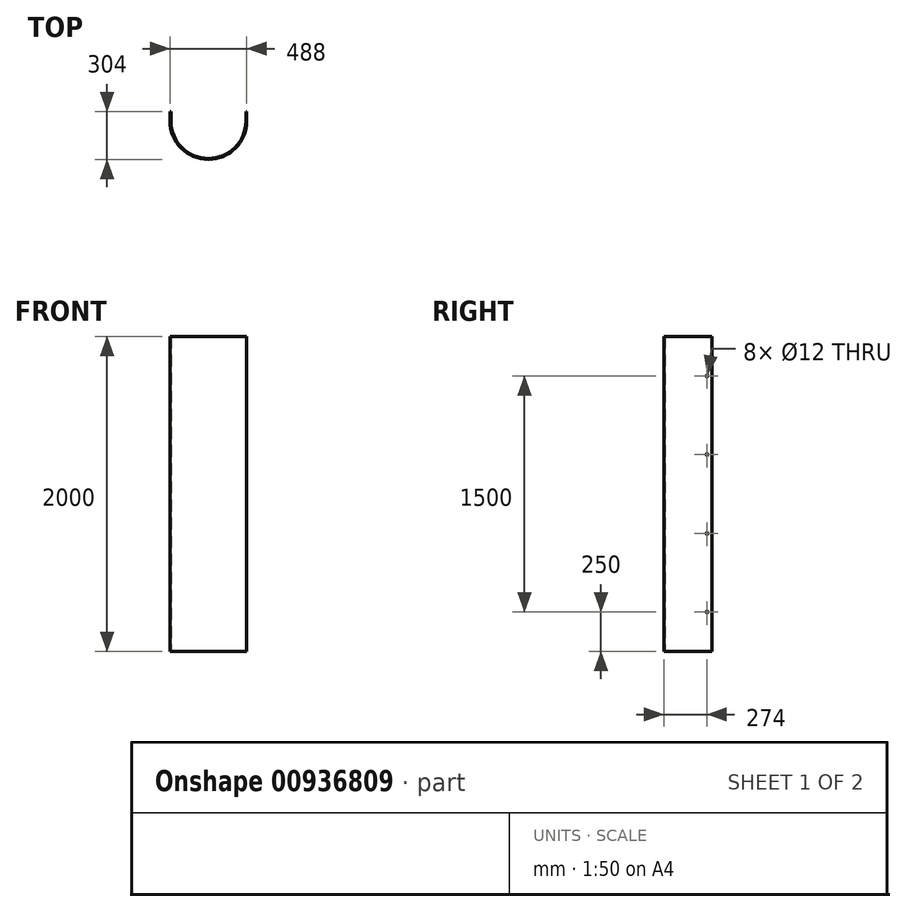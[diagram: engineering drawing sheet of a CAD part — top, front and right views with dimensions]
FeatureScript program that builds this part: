
annotation { "Feature Type Name" : "Feature", "Feature Type Description" : "" }
export const myFeature = defineFeature(function(context is Context, id is Id, definition is map)
    precondition{}
    {
        {
            var Q0;
            Q0=qCreatedBy(makeId("Top.planeOp"),FACE);
            var sketch = newSketch(context, id + "F0", { "sketchPlane" : qUnion([Q0])});
            skArc(sketch, "E0", {"start": v(-238, 0) * mm, "mid": v(0, -238) * mm, "end": v(238, 0) * mm});
            skArc(sketch, "E1.0", {"start": v(-244, 0) * mm, "mid": v(0, -244) * mm, "end": v(244, 0) * mm});
            skLineSegment(sketch, "E2", {"start": v(244, 0) * mm, "end": v(244, 60) * mm});
            skLineSegment(sketch, "E3", {"start": v(244, 60) * mm, "end": v(238, 60) * mm});
            skLineSegment(sketch, "E4", {"start": v(238, 60) * mm, "end": v(238, 0) * mm});
            skLineSegment(sketch, "E5", {"start": v(-244, 0) * mm, "end": v(-244, 60) * mm});
            skLineSegment(sketch, "E6", {"start": v(-244, 60) * mm, "end": v(-238, 60) * mm});
            skLineSegment(sketch, "E7", {"start": v(-238, 60) * mm, "end": v(-238, 0) * mm});
            skSolve(sketch);
        }
        {
            var Q0;
            Q0=makeQuery(id+"F0.imprint","IMPRINT",FACE,{"disambiguationData":[TD([[makeQuery(id+"F0.imprint","IMPRINT",EDGE,{"derivedFrom":sQuery(id+"F0.wireOp",EDGE,"E0")}),-1.0]])]});
            extrude(context, id + "F1", {"entities" : qUnion([Q0]), "depth" : 2000 * mm, "offsetDistance" : 25 * mm});
        }
        {
            var Q0;
            Q0=makeQuery(id+"F1.opExtrude","SWEPT_FACE",FACE,{"disambiguationData":[OSD([sQuery(id+"F0.wireOp",EDGE,"E2")])]});
            var sketch = newSketch(context, id + "F2", { "sketchPlane" : qUnion([Q0])});
            skLineSegment(sketch, "E8.0", {"start": v(60, 2000) * mm, "end": v(60, 0) * mm});
            skLineSegment(sketch, "E9.0", {"start": v(0, 2000) * mm, "end": v(60, 2000) * mm});
            skCircle(sketch, "E10", {"center": v(30, 1750) * mm, "radius": 6 * mm});
            skCircle(sketch, "E11.0.1.0", {"center": v(30, 1250) * mm, "radius": 6 * mm});
            skCircle(sketch, "E11.0.2.0", {"center": v(30, 750) * mm, "radius": 6 * mm});
            skCircle(sketch, "E11.0.3.0", {"center": v(30, 250) * mm, "radius": 6 * mm});
            skLineSegment(sketch, "E11.direction1", {"start": v(30, 1750) * mm, "end": v(55, 1750) * mm, "construction": true});
            skLineSegment(sketch, "E11.direction2", {"start": v(30, 1750) * mm, "end": v(30, 1250) * mm, "construction": true});
            skSolve(sketch);
        }
        {
            var Q0;
            Q0=makeQuery(id+"F2.imprint","IMPRINT",FACE,{"disambiguationData":[TD([[makeQuery(id+"F2.imprint","IMPRINT",EDGE,{"derivedFrom":sQuery(id+"F2.wireOp",EDGE,"E10")}),1.0]])]});
            var Q1;
            Q1=makeQuery(id+"F2.imprint","IMPRINT",FACE,{"disambiguationData":[TD([[makeQuery(id+"F2.imprint","IMPRINT",EDGE,{"derivedFrom":sQuery(id+"F2.wireOp",EDGE,"E11.0.1.0")}),1.0]])]});
            var Q2;
            Q2=makeQuery(id+"F2.imprint","IMPRINT",FACE,{"disambiguationData":[TD([[makeQuery(id+"F2.imprint","IMPRINT",EDGE,{"derivedFrom":sQuery(id+"F2.wireOp",EDGE,"E11.0.2.0")}),1.0]])]});
            var Q3;
            Q3=makeQuery(id+"F2.imprint","IMPRINT",FACE,{"disambiguationData":[TD([[makeQuery(id+"F2.imprint","IMPRINT",EDGE,{"derivedFrom":sQuery(id+"F2.wireOp",EDGE,"E11.0.3.0")}),1.0]])]});
            extrude(context, id + "F3", {"entities" : qUnion([Q0, Q1, Q2, Q3]), "operationType" : NewBodyOperationType.REMOVE, "endBound" : BoundingType.THROUGH_ALL, "oppositeDirection" : true, "depth" : 25 * mm, "offsetDistance" : 25 * mm});
        }
    });
